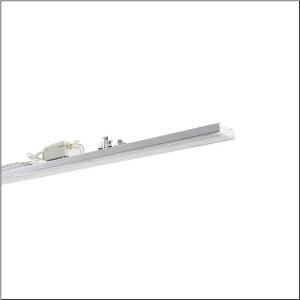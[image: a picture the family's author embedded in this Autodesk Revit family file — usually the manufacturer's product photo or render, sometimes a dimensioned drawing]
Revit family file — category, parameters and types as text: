
# Revit family: licross_r__21_recessed_mo_52te12dv4dxg_0a71
name_source: partatom
category: Lighting Fixtures
units: mm (PartAtom-declared; Revit-internal decimal feet)

## family parameters
Cut with Voids When Loaded = No
Host = Face
Light Source = No
Part Type = Normal
Room Calculation Point = No
Round Connector Dimension = Use Diameter
Shared = No

## types (1)
- --- (1 x LED, 13000 lm, 71 W, 4000K)
    Apparent Load = 71 VA
    CIE Flux Codes = 72 92 99 100 100
    Color Rendering = 80
    Color Temperature = 4000K
    Default Elevation = 1800 mm
    Description = Licross® 21 Recessed MO, luminaire insert, of sheet steel, galvanised, coil coated, white, length: 2.250mm, width: 66mm, height: 67mm, LED rated luminous flux: 13.000lm, light colour: 840, control gear: DALI 2, with plug, 5-pole, with phase selection, mains connection: 220..240V, AC, 50/60Hz, rated input power: 71W, halogen-free wiring, primary optical cover: cover, of PMMA, light emission: direct distribution, primary light characteristic: symmetric, protection rating (complete): IP54, insulation class (complete): insulation class I (protective earthing), certification: CE, ENEC, VDE, UKCA, protection symbol: D if used in an environment with non-conductive dust loads with corresponding accessories, impact resistance: IK06, permissible ambient temperature for indoor applications: -25..+35°C, corresponds to IFS (International Featured Standards) requirements for safety and quality in the food industry, reducing of maximum allowable ambient temperature of 5°C with ceiling mounting, LABS conformity tested according to VDMA 24364:2018-05, packaging unit: 1 piece
    Height = 58 mm
    Lamp = 1 x LED
    Lamp Light Flux = 13000 lm
    Lamp Power = 71 W
    Lamp count = 1
    Length = 2250 mm
    Luminous efficacy = 183 lm/W
    Manufacturer = Siteco
    ModVariant = No
    Model = 52TE12DV4DXG
    Mounting Place = Ceiling
    Mounting Type = Pendant
    Number of Poles = 1
    OnlyDefault = Yes
    Power Factor = 1
    Product Name = Licross® 21 Recessed MO
    Product group = luminaire insert
    ProductGroupID = 901
    Protection Class = Protection class I
    Protection Degree = IP 54
    RLX_Detail_Level = 1
    RLX_Emergency_Light_Flux = 0 lm
    RLX_Emergency_Type = 0
    RLX_Emergency_Type_DB = No
    RlxData = <blob elided: 29565 chars, md5=9638d62a>
    Socket = socket
    Standby Power = 0 W
    System Light Flux = 13000 lm
    System Power = 71 W
    Type Comments = factory setting: luminous flux: 100 % | dim-lin: 254 | 324 mA
    Type Image = l_1296930.jpg
    URL = http://relux.com
    VarID = @adj_057905
    Voltage = 0 V
    Weight = 0.00 kg
    Width = 66 mm

## geometry (parser evidence)
native form markers: Blend x4, Sweep x10
no freeform markers — native parametric forms only
